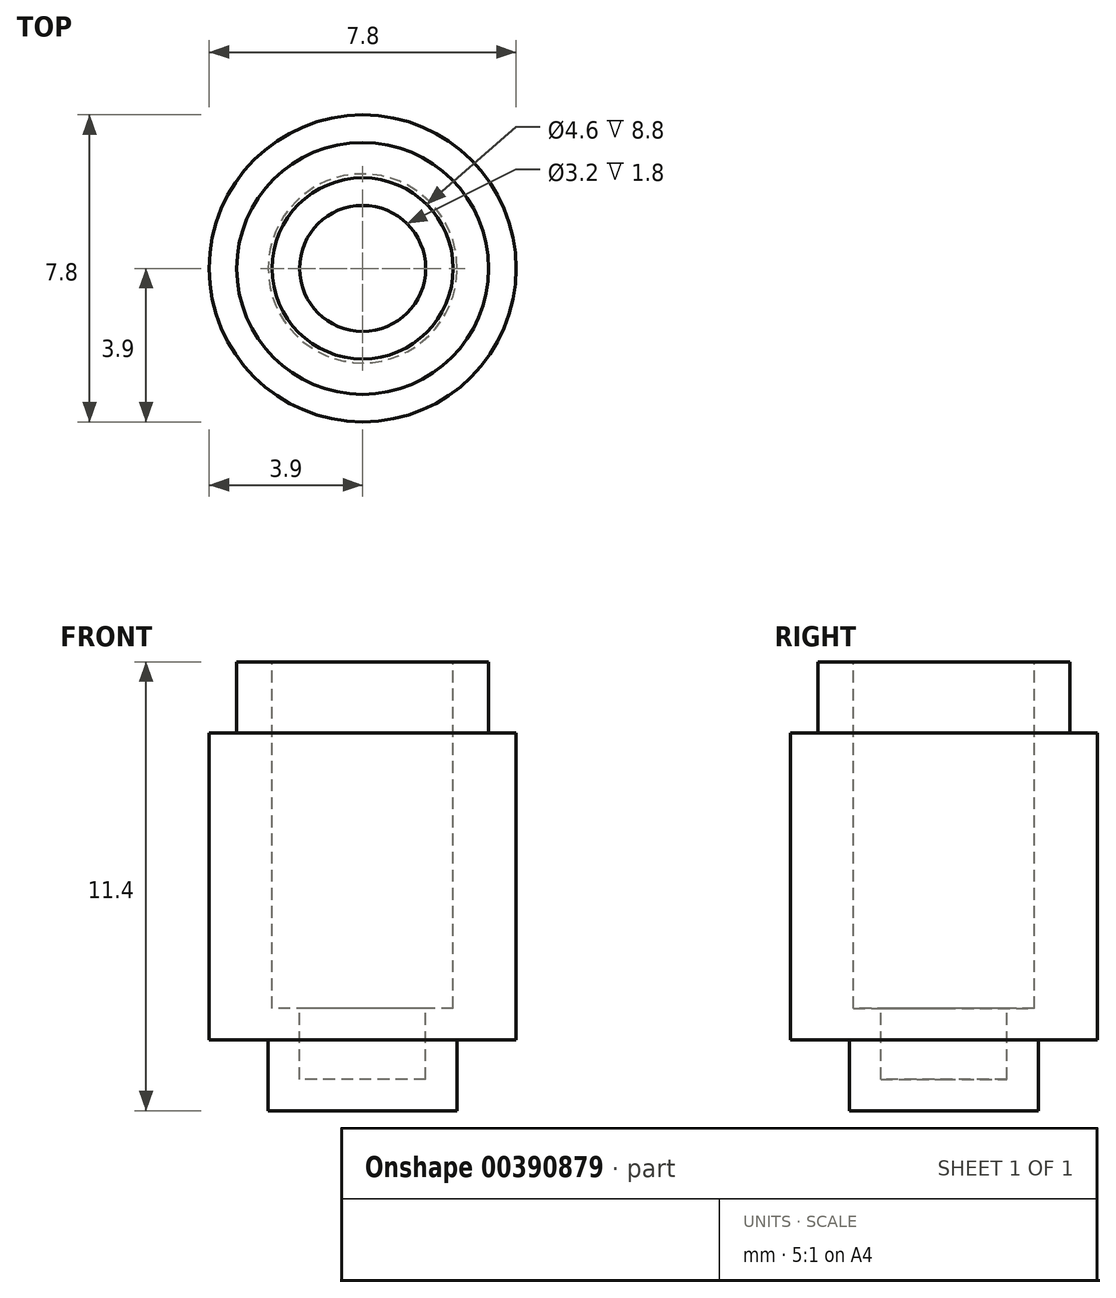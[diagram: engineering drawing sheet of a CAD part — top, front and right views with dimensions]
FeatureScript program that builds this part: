
annotation { "Feature Type Name" : "Feature", "Feature Type Description" : "" }
export const myFeature = defineFeature(function(context is Context, id is Id, definition is map)
    precondition{}
    {
        {
            var Q0;
            Q0=qCreatedBy(makeId("Top.planeOp"),FACE);
            var sketch = newSketch(context, id + "F0", { "sketchPlane" : qUnion([Q0])});
            skCircle(sketch, "E0", {"center": v(0, 0) * mm, "radius": 2.4 * mm});
            skSolve(sketch);
        }
        {
            var Q0;
            Q0=makeQuery(id+"F0.imprint","IMPRINT",FACE,{"disambiguationData":[TD([[makeQuery(id+"F0.imprint","IMPRINT",EDGE,{"derivedFrom":sQuery(id+"F0.wireOp",EDGE,"E0")}),1.0]])]});
            var Q1;
            Q1 = qSketchRegion(id + "F2", true);
            extrude(context, id + "F1", {"entities" : qUnion([Q0, Q1]), "depth" : 1.8 * mm});
        }
        {
            var Q0;
            Q0=makeQuery(id+"F1.opExtrude","CAP_FACE",FACE,{"disambiguationData":[OSD([sQuery(id+"F0.wireOp",EDGE,"E0")])],"isStart":false});
            var sketch = newSketch(context, id + "F2", { "sketchPlane" : qUnion([Q0])});
            skCircle(sketch, "E1", {"center": v(0, 0) * mm, "radius": 3.9 * mm});
            skSolve(sketch);
        }
        {
            var Q0;
            Q0=makeQuery(id+"F2.imprint","IMPRINT",FACE,{"disambiguationData":[TD([[makeQuery(id+"F2.imprint","IMPRINT",EDGE,{"derivedFrom":sQuery(id+"F2.wireOp",EDGE,"E1")}),1.0]])]});
            var Q1;
            Q1=makeQuery(id+"F2.imprint","IMPRINT",FACE,{"disambiguationData":[TD([[makeQuery(id+"F2.imprint","IMPRINT",EDGE,{"derivedFrom":makeQuery(id+"F1.opExtrude","CAP_EDGE",EDGE,{"disambiguationData":[OSD([sQuery(id+"F0.wireOp",EDGE,"E0")])],"isStart":false})}),1.0]])]});
            var Q2;
            Q2 = qSketchRegion(id + "F4", true);
            extrude(context, id + "F3", {"entities" : qUnion([Q0, Q1, Q2]), "operationType" : NewBodyOperationType.ADD, "depth" : 9.6 * mm});
        }
        {
            var Q0;
            Q0=makeQuery(id+"F3.opExtrude","CAP_FACE",FACE,{"disambiguationData":[OSD([sQuery(id+"F2.wireOp",EDGE,"E1")])],"isStart":false});
            var sketch = newSketch(context, id + "F4", { "sketchPlane" : qUnion([Q0])});
            skCircle(sketch, "E2", {"center": v(0, 0) * mm, "radius": 3.2 * mm});
            skSolve(sketch);
        }
        {
            var Q0;
            Q0=makeQuery(id+"F4.imprint","IMPRINT",FACE,{"disambiguationData":[TD([[makeQuery(id+"F4.imprint","IMPRINT",EDGE,{"derivedFrom":sQuery(id+"F4.wireOp",EDGE,"E2")}),-1.0]])]});
            extrude(context, id + "F5", {"entities" : qUnion([Q0]), "operationType" : NewBodyOperationType.REMOVE, "oppositeDirection" : true, "depth" : 1.8 * mm});
        }
        {
            var Q0;
            Q0=makeQuery(id+"F3.opExtrude","CAP_FACE",FACE,{"disambiguationData":[OSD([sQuery(id+"F2.wireOp",EDGE,"E1")])],"isStart":false});
            var sketch = newSketch(context, id + "F6", { "sketchPlane" : qUnion([Q0])});
            skCircle(sketch, "E3", {"center": v(0, 0) * mm, "radius": 2.3 * mm});
            skSolve(sketch);
        }
        {
            var Q0;
            Q0=makeQuery(id+"F6.imprint","IMPRINT",FACE,{"disambiguationData":[TD([[makeQuery(id+"F6.imprint","IMPRINT",EDGE,{"derivedFrom":sQuery(id+"F6.wireOp",EDGE,"E3")}),1.0]])]});
            var Q1;
            Q1=sQuery(id+"F6.wireOp",EDGE,"E3");
            extrude(context, id + "F7", {"entities" : qUnion([Q0]), "operationType" : NewBodyOperationType.REMOVE, "surfaceEntities" : qUnion([Q1]), "oppositeDirection" : true, "depth" : 8.8 * mm});
        }
        {
            var Q0;
            Q0=makeQuery(id+"F7.boolean.opBoolean","COPY",FACE,{"derivedFrom":makeQuery(id+"F7.opExtrude","CAP_FACE",FACE,{"disambiguationData":[OSD([sQuery(id+"F6.wireOp",EDGE,"E3")])],"isStart":false})});
            var sketch = newSketch(context, id + "F8", { "sketchPlane" : qUnion([Q0])});
            skCircle(sketch, "E4", {"center": v(0, 0) * mm, "radius": 1.6 * mm});
            skSolve(sketch);
        }
        {
            var Q0;
            Q0 = qSketchRegion(id + "F8", true);
            extrude(context, id + "F9", {"entities" : qUnion([Q0]), "operationType" : NewBodyOperationType.REMOVE, "oppositeDirection" : true, "depth" : 1.8 * mm});
        }
    });
